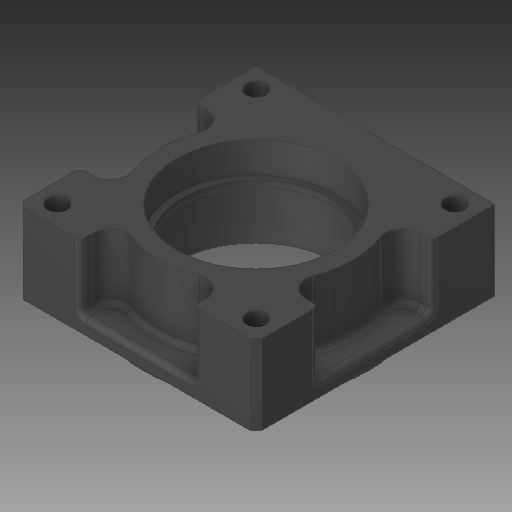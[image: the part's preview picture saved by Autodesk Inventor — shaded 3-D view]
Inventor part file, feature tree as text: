
AUTODESK INVENTOR PART (.ipt)
format: ipt  version: 2019 (Build 230136000, 136)  size: 230,400 bytes
history: native  units: in
note: dims shown in document units (in); Inventor stores cm internally (conversion verified against a paired STEP export)
features: chamfer x1
ambient origin geometry x8: Origin, YZ Plane, XZ Plane, XY Plane, X Axis, Y Axis, Z Axis, Center Point
bodies: Solid1 (feature_tree)
feature tree (1):
  chamfer  "Chamfer2"  [1 undecoded]
note: 1 required parameter value undecoded (feature->parameter linkage not recoverable at this tier; creation-order binding heuristic only, values carry confidence <= 0.55)
